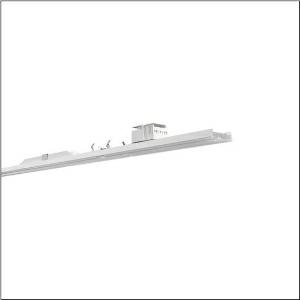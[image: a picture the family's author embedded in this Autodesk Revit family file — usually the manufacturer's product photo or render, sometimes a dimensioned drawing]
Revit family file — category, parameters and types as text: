
# Revit family: licross_r__11_recessed_mo_51tl11dn49xf_705e
name_source: partatom
category: Lighting Fixtures
units: mm (PartAtom-declared; Revit-internal decimal feet)

## family parameters
Cut with Voids When Loaded = No
Host = Face
Light Source = No
Part Type = Normal
Room Calculation Point = No
Round Connector Dimension = Use Diameter
Shared = No

## types (1)
- --- (1 x LED, 9030 lm, 55.4 W, 4000K)
    Apparent Load = 55 VA
    CIE Flux Codes = 89 96 99 100 100
    Color Rendering = 80
    Color Temperature = 4000K
    Default Elevation = 1800 mm
    Description = Licross® 11 Recessed MOluminaire insert, length: 1.500mm, width: 66mm, height: 67mm, LED rated luminous flux: 9.030lm, light colour: 840, control gear: DALI 2, control gear: ECG DALI, with plug, 5-pole, with phase selection, mains connection: 220..240V, AC, 50/60Hz, halogen-free wiring, primary optical cover: cover, of PMMA, light emission: direct distribution, protection rating (complete): IP40, insulation class (complete): insulation class I (protective earthing), certification: CE, ENEC, VDE, protection symbol: D if used in an environment without relevant dust loads with corresponding accessories, permissible ambient temperature for indoor applications: -25..+40°C, reducing of maximum allowable ambient temperature of 5°C with ceiling mounting, corresponds to IFS (International Featured Standards) requirements for safety and quality in the food industry, packaging unit: 1 piece
    Height = 58 mm
    Lamp = 1 x LED
    Lamp Light Flux = 9030 lm
    Lamp Power = 55.4 W
    Lamp count = 1
    Length = 1500 mm
    Luminous efficacy = 163 lm/W
    Manufacturer = Siteco
    ModVariant = No
    Model = 51TL11DN49XF
    Mounting Place = Ceiling
    Mounting Type = Pendant
    Number of Poles = 1
    OnlyDefault = Yes
    Power Factor = 1
    Product Name = Licross® 11 Recessed MO
    Product group = luminaire insert
    ProductGroupID = 902
    Protection Class = Protection class I
    Protection Degree = IP 40
    RLX_Detail_Level = 1
    RlxData = <blob elided: 22101 chars, md5=dd105f53>
    Socket = socket
    Standby Power = 0 W
    System Light Flux = 9030 lm
    System Power = 55 W
    Type Comments = factory setting: luminous flux: 100 % | dim-lin: 254 | 365 mA
    Type Image = l_1266722.jpg
    URL = http://relux.com
    VarID = @adj_138731
    Voltage = 0 V
    Weight = 0.00 kg
    Width = 66 mm

## geometry (parser evidence)
native form markers: Blend x4, Sweep x12
no freeform markers — native parametric forms only
